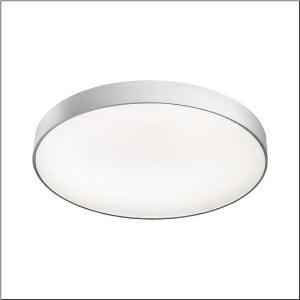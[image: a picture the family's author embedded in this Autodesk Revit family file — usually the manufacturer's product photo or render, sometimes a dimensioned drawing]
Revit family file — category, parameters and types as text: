
# Revit family: round_21_l_51mr38nd0321s
name_source: partatom
category: Lighting Fixtures
units: mm (PartAtom-declared; Revit-internal decimal feet)

## family parameters
Cut with Voids When Loaded = No
Host = Face
Light Source = No
Part Type = Normal
Room Calculation Point = No
Round Connector Dimension = Use Diameter
Shared = No

## types (1)
- Round 21 L (1 x LED, 11740 lm, 88.2 W, 3000K)
    Apparent Load = 88 VA
    CIE Flux Codes = 66 90 98 71 100
    Color Rendering = 80
    Color Temperature = 3000K
    Default Elevation = 1800 mm
    Description = Round 21 L, wall and ceiling luminaire, primary optical cover: micro prismatic cover, of PMMA, transparent, CAT 2 (L<= 3000cd/m²), light emission: direct/indirect distribution, primary light characteristic: symmetric, installation type: suspended mounting, surface-mounted, LED, rated luminous flux: 9.230lm, luminous efficacy: 111lm/W, light colour: 830, colour temperature: 3000K, with terminal, 5-pole, mains connection: 230V, AC, 50/60Hz, rated input power: 83W, housing, of aluminium, coated, silver, diameter: 850mm, height: 62mm, protection rating (complete): IP40, insulation class (complete): insulation class I (protective earthing), certification: CE, impact resistance: IK04, permissible operating ambient temperature: -10..+35°C, packaging unit: 1 piece
    Height = 87 mm
    Lamp = 1 x LED
    Lamp Light Flux = 11740 lm
    Lamp Power = 88.2 W
    Lamp count = 1
    Length = 850 mm
    Luminous efficacy = 133 lm/W
    Manufacturer = Siteco
    ModVariant = No
    Model = 51MR38ND0321S
    Mounting Place = Ceiling
    Mounting Type = Surface mounted
    Number of Poles = 1
    OnlyDefault = Yes
    Power Factor = 1
    Product Name = Round 21 L
    Product group = wall and ceiling luminaire
    ProductGroupID = 303
    Protection Class = Protection class I
    Protection Degree = IP 40
    RLX_Detail_Level = 1
    RLX_Emergency_Light_Flux = 0 lm
    RLX_Emergency_Type = 0
    RLX_Emergency_Type_DB = No
    RlxData = <blob elided: 25225 chars, md5=4e6ff271>
    Socket = socket
    Standby Power = 0 W
    System Light Flux = 11740 lm
    System Power = 88 W
    Type Comments = Product without accessories
    Type Image = l_1258322.jpg
    URL = http://relux.com
    VarID = ---
    Voltage = 0 V
    Weight = 0.00 kg
    Width = 0 mm  [stored 0 ft]

note: [stored X ft] marks values corroborated as IEEE doubles in the binary element streams (Revit-internal decimal feet)

## geometry (parser evidence)
native form markers: Blend x4, Sweep x16
no freeform markers — native parametric forms only
